# Revit family: FU_Chair_Sandler_Palm Beach 5-2
name_source: partatom
category: Furniture
units: mm (PartAtom-declared; Revit-internal decimal feet)

## family parameters
Always vertical = Yes
Cut with Voids When Loaded = No
OmniClass Number = 23.40.20.00
OmniClass Title = General Furniture and Specialties
Room Calculation Point = No
Shared = No
Work Plane-Based = No

## types (1)
- Palm Beach 5.2
    Default Elevation = 0 mm  [stored 0 ft]
    Depth = 585 mm  [stored 1.91929 ft]
    Description = Easy Chair with solid beech frame, and upholstered back with square button pattern.
    Frame = Wood - Beech - 5018 Turquoise Blue
    Height = 885 mm
    Manufacturer = Sandler
    Model = Palm Beach 5.2
    Seat = Leather - Sandler 145
    URL = https://www.sandlerseating.com
    Width = 565 mm  [stored 1.85367 ft]

note: [stored X ft] marks values corroborated as IEEE doubles in the binary element streams (Revit-internal decimal feet)

## geometry (parser evidence)
native form markers: Sweep x4
no freeform markers — native parametric forms only
